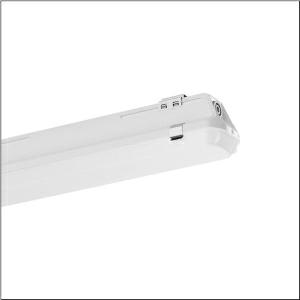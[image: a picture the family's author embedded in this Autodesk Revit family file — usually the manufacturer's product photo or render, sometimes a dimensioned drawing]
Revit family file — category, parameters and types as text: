
# Revit family: monsun_r__21_emergency_51fb10dp468b2_8461
name_source: partatom
category: Lighting Fixtures
units: mm (PartAtom-declared; Revit-internal decimal feet)

## family parameters
Cut with Voids When Loaded = No
Host = Face
Light Source = No
Part Type = Normal
Room Calculation Point = No
Round Connector Dimension = Use Diameter
Shared = No

## types (1)
- --- (1 x LED, 940 lm, 7.3 W, 4000K)
    Apparent Load = 7 VA
    CIE Flux Codes = 47 77 93 94 100
    Color Rendering = 80
    Color Temperature = 4000K
    Default Elevation = 1800 mm
    Description = Monsun® 21 emergency, damp-proof luminaire, chain hanger, primary optical cover: enclosure, of PMMA, light emission: direct distribution, primary light characteristic: symmetric, installation type: suspended mounting, surface-mounted, horizontal mounting, vertical mounting, LED, rated luminous flux: 6.060lm, luminous efficacy: 154lm/W, light colour: 840, colour temperature: 4000K, control gear: ECG DALI, with terminal, 5-pole, max. 2.5mm², mains connection: 220..240V, AC/DC, 0/50..60Hz, rated input power: 39W, housing, of glass-fibre reinforced polyester, uncoated, bright grey, incl. chain hanger, length: 1.590mm, width: 90mm, height: 88mm, clip for enclosure, of stainless steel (V2A), ceiling mounting element, of stainless steel (V2A), chain hanger, of stainless steel (V2A), protection rating (complete): IP66, insulation class (complete): insulation class I (protective earthing), certification: CE, UKCA, protection symbol: D, impact resistance: IK04, permissible operating ambient temperature: -25..+35°C, standard: EN 50419, EN 60598-2-1, EN 60598-2-22, corresponds to IFS (International Featured Standards) requirements for safety and quality in the food industry, for indoor or canopied outdoor use, no direct snow, no direct sun, no direct rain, contact your sales advisor before using the luminaires in applications with unclear chemical exposure, large temperature fluctuations or condensation-forming humidity, LABS conformity tested according to VDMA 24364:2018-05, packaging unit: 1 piece
    Height = 89 mm
    Lamp = 1 x LED
    Lamp Light Flux = 940 lm
    Lamp Power = 7.3 W
    Lamp count = 1
    Length = 1590 mm
    Luminous efficacy = 129 lm/W
    Manufacturer = Siteco
    ModVariant = No
    Model = 51FB10DP468B2
    Mounting Place = Ceiling
    Mounting Type = Surface mounted
    Number of Poles = 1
    OnlyDefault = Yes
    Power Factor = 1
    Product Name = Monsun® 21 emergency
    Product group = damp-proof luminaire
    ProductGroupID = 300
    Protection Class = Protection class I
    Protection Degree = IP 66
    RLX_Detail_Level = 1
    RLX_Emergency_Light_Flux = 0 lm
    RLX_Emergency_Type = 0
    RLX_Emergency_Type_DB = No
    RlxData = <blob elided: 92641 chars, md5=66ca8800>
    Socket = socket
    Standby Power = 0 W
    System Light Flux = 940 lm
    System Power = 7 W
    Type Comments = : equivalent power supply (DC)
    Type Image = l_1006717.jpg
    URL = http://relux.com
    VarID = @adj_134215
    Voltage = 0 V
    Weight = 0.00 kg
    Width = 90 mm

## geometry (parser evidence)
native form markers: Blend x4, Sweep x14
no freeform markers — native parametric forms only
